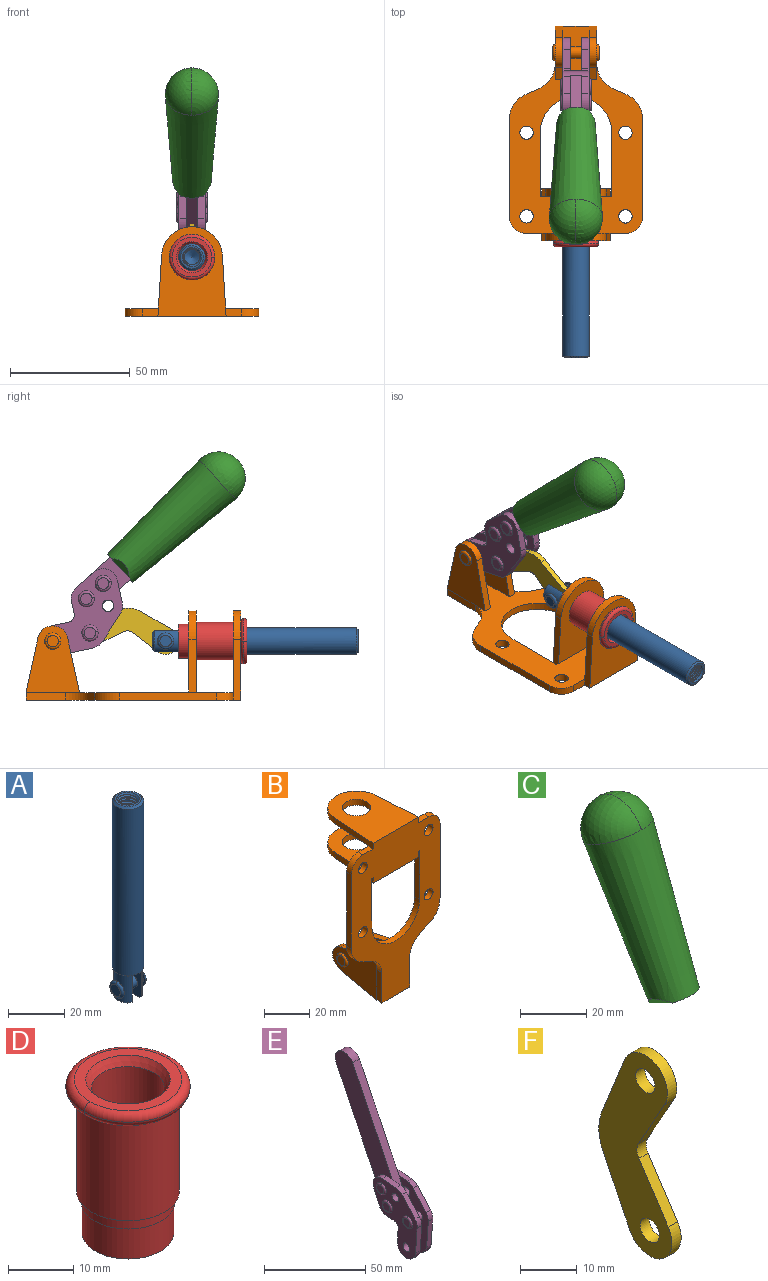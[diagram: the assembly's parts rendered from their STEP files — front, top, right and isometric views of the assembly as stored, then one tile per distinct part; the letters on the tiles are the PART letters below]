
ASSEMBLY  parts=6 mates=6
PART A: 48 faces, bbox 12.6x11.1x86.1 mm
  f0: torus R=2.41mm, axis (-1,0,0), area 15mm2, adj f30,f32,f34
  f1: torus R=2.41mm, axis (-1,0,0), area 15mm2, adj f29,f31,f33
  f2: cylinder r=5.54mm len=72.39mm, axis (0,0,1), area 2518.5mm2, adj f3,f4,f42,f43
  f3: cone r=5.54mm half-angle=45deg, axis (0,0,1), area 7.6mm2, adj f2,f5,f41
  f4: cone r=5.54mm half-angle=45deg, axis (0,0,-1), area 34.9mm2, adj f2,f39
  f5: cylinder r=5.08mm len=11.48mm, axis (0,0,1), area 108.3mm2, adj f3,f7,f8,f41
  f6: cylinder r=2.41mm len=4.83mm, axis (-1,0,0), area 71.2mm2, adj f40,f41
  f7: cylinder r=2.41mm len=4.83mm, axis (-1,0,0), area 7.6mm2, adj f5,f34
  f8: cone r=5.08mm half-angle=45deg, axis (0,0,1), area 10.6mm2, adj f5,f37,f41
  f9: cone r=3.98mm half-angle=45deg, axis (0,0,1), area 17.6mm2, adj f27,f39,f45,f46,f47
  f10: cylinder r=2.41mm len=4.83mm, axis (-1,0,0), area 7.6mm2, adj f33,f38
  f11: cylinder r=3.2mm len=6.4mm, axis (0,0,1), area 78.4mm2, adj f12,f28,f44,f45,f47
  f12: cylinder r=3.2mm len=6.4mm, axis (0,0,1), area 10.5mm2, adj f11,f13,f45,f47
  f13: cylinder r=3.2mm len=6.4mm, axis (0,0,1), area 10.5mm2, adj f12,f14,f45,f47
  f14: cylinder r=3.2mm len=6.4mm, axis (0,0,1), area 10.5mm2, adj f13,f15,f45,f47
  f15: cylinder r=3.2mm len=6.4mm, axis (0,0,1), area 10.5mm2, adj f14,f16,f45,f47
  f16: cylinder r=3.2mm len=6.4mm, axis (0,0,1), area 10.5mm2, adj f15,f17,f45,f47
  f17: cylinder r=3.2mm len=6.4mm, axis (0,0,1), area 10.5mm2, adj f16,f18,f45,f47
  f18: cylinder r=3.2mm len=6.4mm, axis (0,0,1), area 10.5mm2, adj f17,f19,f45,f47
  f19: cylinder r=3.2mm len=6.4mm, axis (0,0,1), area 10.5mm2, adj f18,f20,f45,f47
  f20: cylinder r=3.2mm len=6.4mm, axis (0,0,1), area 10.5mm2, adj f19,f21,f45,f47
  f21: cylinder r=3.2mm len=6.4mm, axis (0,0,1), area 10.5mm2, adj f20,f22,f45,f47
  f22: cylinder r=3.2mm len=6.4mm, axis (0,0,1), area 10.5mm2, adj f21,f23,f45,f47
  f23: cylinder r=3.2mm len=6.4mm, axis (0,0,1), area 10.5mm2, adj f22,f24,f45,f47
  f24: cylinder r=3.2mm len=6.4mm, axis (0,0,1), area 10.5mm2, adj f23,f25,f45,f47
  f25: cylinder r=3.2mm len=6.4mm, axis (0,0,1), area 10.5mm2, adj f24,f26,f45,f47
  f26: cylinder r=3.2mm len=6.4mm, axis (0,0,1), area 10.5mm2, adj f25,f27,f45,f47
  f27: cylinder r=3.2mm len=6.4mm, axis (0,0,1), area 7.4mm2, adj f9,f26,f45,f47
  f28: cone r=3.2mm half-angle=60deg, axis (0,0,1), area 37.2mm2, adj f11
  f29: plane 4.83x4.83mm, normal (-1,0,0), area 18.3mm2, adj f1,f31
  f30: plane 4.83x4.83mm, normal (1,0,0), area 18.3mm2, adj f0,f32
  f31: torus R=2.41mm, axis (-1,0,0), area 15mm2, adj f1,f29,f33
  f32: torus R=2.41mm, axis (-1,0,0), area 15mm2, adj f0,f30,f34
  f33: plane 6.83x6.83mm, normal (1,0,0), area 18.3mm2, adj f1,f10,f31
  f34: plane 6.83x6.83mm, normal (-1,0,0), area 18.3mm2, adj f0,f7,f32
  f35: cone r=5.08mm half-angle=45deg, axis (0,0,1), area 10.6mm2, adj f36,f38,f40
  f36: plane 7.25x1.97mm, normal (0,0,-1), area 10mm2, adj f35,f40
  f37: plane 7.25x1.97mm, normal (0,0,-1), area 10mm2, adj f8,f41
  f38: cylinder r=5.08mm len=11.48mm, axis (0,0,1), area 108.3mm2, adj f10,f35,f40,f42
  f39: plane 9.55x9.55mm, normal (0,0,1), area 22mm2, adj f4,f9
  f40: plane 12.76x10.09mm, normal (1,0,0), area 95.7mm2, adj f6,f35,f36,f38,f42,f43
  f41: plane 12.76x10.09mm, normal (-1,0,0), area 95.7mm2, adj f3,f5,f6,f8,f37,f43
  f42: cone r=5.54mm half-angle=45deg, axis (0,0,1), area 7.6mm2, adj f2,f38,f40
  f43: plane 11.07x4.7mm, normal (0,0,-1), area 50.4mm2, adj f2,f40,f41
  f44: plane 0.89x0.62mm, normal (-1,0,0), area 0.3mm2, adj f11,f45,f46,f47
  f45: bspline ~24.8x7.63mm, area 266.6mm2, adj f9,f11,f12,f13,f14,f15,f16,f17
  f46: bspline ~24.87x7.63mm, area 73.6mm2, adj f9,f44,f45,f47
  f47: bspline ~24.98x7.63mm, area 272.5mm2, adj f9,f11,f12,f13,f14,f15,f16,f17
PART B: 55 faces, bbox 55.7x37.4x89.8 mm
  f0: torus R=2.41mm, axis (-1,0,0), area 15mm2, adj f11,f15,f25
  f1: torus R=2.41mm, axis (-1,0,0), area 15mm2, adj f10,f12,f22
  f2: cylinder r=2.78mm len=5.56mm, axis (0,-1,0), area 54.2mm2, adj f30,f54
  f3: cylinder r=14.99mm len=29.97mm, axis (0,-1,0), area 145.9mm2, adj f30,f49,f53,f54
  f4: cylinder r=2.78mm len=5.56mm, axis (0,-1,0), area 54.2mm2, adj f30,f54
  f5: cylinder r=2.78mm len=5.56mm, axis (0,-1,0), area 54.2mm2, adj f30,f54
  f6: cylinder r=2.78mm len=5.56mm, axis (0,-1,0), area 54.2mm2, adj f30,f54
  f7: cylinder r=6.35mm len=12.7mm, axis (0,0,1), area 123.6mm2, adj f27,f51
  f8: cylinder r=6.35mm len=12.7mm, axis (0,0,-1), area 124.7mm2, adj f21,f35
  f9: cylinder r=2.41mm len=11.18mm, axis (-1,0,0), area 169.4mm2, adj f16,f19
  f10: plane 4.83x4.83mm, normal (1,0,0), area 18.3mm2, adj f1,f12
  f11: plane 4.83x4.83mm, normal (-1,0,0), area 18.3mm2, adj f0,f15
  f12: torus R=2.41mm, axis (-1,0,0), area 15mm2, adj f1,f10,f22
  f13: cylinder r=6.35mm len=12.41mm, axis (1,0,0), area 53.4mm2, adj f18,f19,f22,f23
  f14: cylinder r=6.35mm len=12.41mm, axis (-1,0,0), area 53.4mm2, adj f16,f17,f24,f25
  f15: torus R=2.41mm, axis (-1,0,0), area 15mm2, adj f0,f11,f25
  f16: plane 27.86x22.35mm, normal (1,0,0), area 425.4mm2, adj f9,f14,f17,f24,f30
  f17: plane 22.86x4.97mm, normal (0,0.21,0.98), area 72.5mm2, adj f14,f16,f25,f30
  f18: plane 22.86x4.97mm, normal (0,0.21,0.98), area 72.5mm2, adj f13,f19,f22,f30
  f19: plane 27.86x22.35mm, normal (-1,0,0), area 425.4mm2, adj f9,f13,f18,f23,f30
  f20: cylinder r=12.7mm len=25.35mm, axis (0,0,-1), area 119.8mm2, adj f21,f34,f35,f36
  f21: plane 34.21x28.07mm, normal (0,0,-1), area 702.4mm2, adj f8,f20,f30,f34,f36
  f22: plane 27.96x22.45mm, normal (1,0,0), area 407.2mm2, adj f1,f12,f13,f18,f23,f30,f42,f43
  f23: plane 22.86x4.97mm, normal (0,0.21,-0.98), area 72.5mm2, adj f13,f19,f22,f44
  f24: plane 22.86x4.97mm, normal (0,0.21,-0.98), area 72.5mm2, adj f14,f16,f25,f44
  f25: plane 27.86x22.35mm, normal (-1,0,0), area 407.1mm2, adj f0,f14,f15,f17,f24,f30,f45,f46
  f26: plane 3.1x0.95mm, normal (0,0,-1), area 2.7mm2, adj f30,f49,f50,f54
  f27: plane 34.21x28.07mm, normal (0,0,1), area 702.4mm2, adj f7,f28,f30,f50,f52
  f28: cylinder r=12.7mm len=25.35mm, axis (0,0,1), area 118.8mm2, adj f27,f50,f51,f52
  f29: plane 3.1x0.95mm, normal (0,0,-1), area 2.7mm2, adj f30,f52,f53,f54
  f30: plane 86.54x55.63mm, normal (0,1,0), area 2362.9mm2, adj f2,f3,f4,f5,f6,f16,f17,f18
  f31: plane 40.56x3.1mm, normal (-1,0,0), area 125.7mm2, adj f30,f32,f48,f54
  f32: cylinder r=7.11mm len=7.11mm, axis (0,-1,0), area 34.6mm2, adj f30,f31,f33,f54
  f33: plane 6.67x3.1mm, normal (0,0,1), area 20.4mm2, adj f30,f32,f34,f54
  f34: plane 25.39x3.13mm, normal (-1,0.06,0), area 79.5mm2, adj f20,f21,f33,f35,f54
  f35: plane 37.31x28.45mm, normal (0,0,1), area 789.9mm2, adj f8,f20,f34,f36,f54
  f36: plane 25.39x3.13mm, normal (1,0.06,0), area 79.5mm2, adj f20,f21,f35,f37,f54
  f37: plane 6.67x3.1mm, normal (0,0,1), area 20.4mm2, adj f30,f36,f38,f54
  f38: cylinder r=7.11mm len=7.11mm, axis (0,-1,0), area 34.6mm2, adj f30,f37,f39,f54
  f39: plane 40.56x3.1mm, normal (1,0,0), area 125.7mm2, adj f30,f38,f40,f54
  f40: cylinder r=11.18mm len=10.16mm, axis (0,-1,0), area 39.5mm2, adj f30,f39,f41,f54
  f41: plane 6.09x3.1mm, normal (0.42,0,-0.91), area 20.8mm2, adj f30,f40,f42,f54
  f42: cylinder r=11.18mm len=9.41mm, axis (0,-1,0), area 37.2mm2, adj f22,f30,f41,f43,f54
  f43: plane 16.5x3.1mm, normal (1,0,0), area 51.1mm2, adj f22,f42,f44,f54
  f44: plane 17.37x3.1mm, normal (0,0,-1), area 53.8mm2, adj f23,f24,f30,f43,f45,f54
  f45: plane 16.5x3.1mm, normal (-1,0,0), area 51.1mm2, adj f25,f44,f46,f54
  f46: cylinder r=11.18mm len=9.41mm, axis (0,-1,0), area 37.2mm2, adj f25,f30,f45,f47,f54
  f47: plane 6.09x3.1mm, normal (-0.42,0,-0.91), area 20.8mm2, adj f30,f46,f48,f54
  f48: cylinder r=11.18mm len=10.16mm, axis (0,-1,0), area 39.5mm2, adj f30,f31,f47,f54
  f49: plane 26.54x3.1mm, normal (-1,0,0), area 82.3mm2, adj f3,f26,f30,f54
  f50: plane 25.39x3.1mm, normal (1,0.06,0), area 78.8mm2, adj f26,f27,f28,f51,f54
  f51: plane 37.31x28.45mm, normal (0,0,-1), area 789.9mm2, adj f7,f28,f50,f52,f54
  f52: plane 25.39x3.1mm, normal (-1,0.06,0), area 78.8mm2, adj f27,f28,f29,f51,f54
  f53: plane 26.54x3.1mm, normal (1,0,0), area 82.3mm2, adj f3,f29,f30,f54
  f54: plane 89.66x55.63mm, normal (0,-1,0), area 2678.5mm2, adj f2,f3,f4,f5,f6,f26,f29,f31
PART C: 11 faces, bbox 22.3x42.6x64.5 mm
  f0: sphere r=11.13mm, area 411.4mm2, adj f1,f8
  f1: cone r=11.11mm half-angle=3.3deg, axis (0,0.44,0.9), area 3251.8mm2, adj f0,f7,f8,f9,f10
  f2: cylinder r=6.16mm len=11.7mm, axis (1,0,0), area 89.5mm2, adj f3,f4,f5,f6
  f3: plane 60.23x36.75mm, normal (-1,0,0), area 763.6mm2, adj f2,f4,f6,f10
  f4: plane 51.37x25.05mm, normal (0,0.9,-0.44), area 264.2mm2, adj f2,f3,f5,f10
  f5: plane 60.23x36.75mm, normal (1,0,0), area 763.6mm2, adj f2,f4,f6,f10
  f6: plane 51.37x25.05mm, normal (0,-0.9,0.44), area 264.2mm2, adj f2,f3,f5,f10
  f7: plane 9.95x5.95mm, normal (0.71,-0.31,-0.64), area 25.8mm2, adj f1,f10
  f8: sphere r=11.13mm, area 411.4mm2, adj f0,f1
  f9: plane 9.95x5.95mm, normal (-0.71,-0.31,-0.64), area 25.8mm2, adj f1,f10
  f10: plane 14.27x11.38mm, normal (0,-0.44,-0.9), area 106.7mm2, adj f1,f3,f4,f5,f6,f7,f9
PART D: 15 faces, bbox 20.6x20.6x28.7 mm
  f0: torus R=8.26mm, axis (0,0,1), area 56.8mm2, adj f1,f10,f12
  f1: torus R=8.26mm, axis (0,0,1), area 56.8mm2, adj f0,f6,f13
  f2: cylinder r=5.59mm len=25.91mm, axis (0,0,1), area 909.6mm2, adj f3,f4
  f3: cone r=6.86mm half-angle=45deg, axis (0,0,-1), area 70.2mm2, adj f2,f14
  f4: cone r=6.47mm half-angle=30deg, axis (0,0,1), area 66.7mm2, adj f2,f13
  f5: cylinder r=7.04mm len=14.07mm, axis (0,0,1), area 252.6mm2, adj f11,f14
  f6: torus R=8.26mm, axis (0,0,1), area 56.8mm2, adj f1,f12,f13
  f7: cylinder r=7.16mm len=14.33mm, axis (0,0,1), area 91.5mm2, adj f9,f11
  f8: cylinder r=7.86mm len=18.42mm, axis (0,0,1), area 909.6mm2, adj f9,f10
  f9: plane 15.72x15.72mm, normal (0,0,-1), area 33mm2, adj f7,f8
  f10: plane 16.51x16.51mm, normal (0,0,-1), area 19.9mm2, adj f0,f8,f12
  f11: plane 14.33x14.33mm, normal (0,0,-1), area 5.7mm2, adj f5,f7
  f12: torus R=8.26mm, axis (0,0,1), area 56.8mm2, adj f0,f6,f10
  f13: plane 16.51x16.51mm, normal (0,0,1), area 82.7mm2, adj f1,f4,f6
  f14: plane 14.07x14.07mm, normal (0,0,-1), area 7.8mm2, adj f3,f5
PART E: 59 faces, bbox 12.9x60.2x99.6 mm
  f0: torus R=2.39mm, axis (-1,0,0), area 14.9mm2, adj f20,f43,f51
  f1: torus R=2.39mm, axis (-1,0,0), area 14.9mm2, adj f19,f42,f51
  f2: torus R=2.39mm, axis (-1,0,0), area 14.9mm2, adj f18,f35,f51
  f3: torus R=2.39mm, axis (-1,0,0), area 14.9mm2, adj f14,f17,f23
  f4: torus R=2.39mm, axis (-1,0,0), area 14.9mm2, adj f13,f16,f23
  f5: torus R=2.39mm, axis (-1,0,0), area 14.9mm2, adj f12,f15,f23
  f6: cylinder r=2.39mm len=4.78mm, axis (1,0,0), area 46.5mm2, adj f48,f50,f51
  f7: cylinder r=2.39mm len=4.78mm, axis (1,0,0), area 46.5mm2, adj f50,f51
  f8: cylinder r=6.35mm len=12.68mm, axis (1,0,0), area 61.8mm2, adj f38,f39,f50,f51
  f9: cylinder r=2.39mm len=4.78mm, axis (-1,0,0), area 70.5mm2, adj f46,f50
  f10: cylinder r=2.39mm len=4.78mm, axis (-1,0,0), area 46.5mm2, adj f23,f45,f46
  f11: cylinder r=2.39mm len=4.78mm, axis (-1,0,0), area 46.5mm2, adj f23,f46
  f12: plane 4.78x4.78mm, normal (1,0,0), area 17.9mm2, adj f5,f15
  f13: plane 4.78x4.78mm, normal (1,0,0), area 17.9mm2, adj f4,f16
  f14: plane 4.78x4.78mm, normal (1,0,0), area 17.9mm2, adj f3,f17
  f15: torus R=2.39mm, axis (-1,0,0), area 14.9mm2, adj f5,f12,f23
  f16: torus R=2.39mm, axis (-1,0,0), area 14.9mm2, adj f4,f13,f23
  f17: torus R=2.39mm, axis (-1,0,0), area 14.9mm2, adj f3,f14,f23
  f18: plane 4.78x4.78mm, normal (-1,0,0), area 17.9mm2, adj f2,f35
  f19: plane 4.78x4.78mm, normal (-1,0,0), area 17.9mm2, adj f1,f42
  f20: plane 4.78x4.78mm, normal (-1,0,0), area 17.9mm2, adj f0,f43
  f21: plane 2.26x0.2mm, normal (1,0,0), area 0.2mm2, adj f31,f44
  f22: plane 2.26x0.2mm, normal (-1,0,0), area 0.2mm2, adj f41,f44
  f23: plane 39.37x30.77mm, normal (1,0,0), area 565.5mm2, adj f3,f4,f5,f10,f11,f15,f16,f17
  f24: cylinder r=6.1mm len=4.15mm, axis (-1,0,0), area 14.7mm2, adj f23,f25,f32,f46
  f25: plane 10.25x9.01mm, normal (0,-0.75,0.66), area 42.3mm2, adj f23,f24,f26,f46
  f26: cylinder r=6.35mm len=4.64mm, axis (-1,0,0), area 15.6mm2, adj f23,f25,f27,f46
  f27: plane 15.84x3.1mm, normal (0,-1,-0.07), area 49.2mm2, adj f23,f26,f28,f46
  f28: cylinder r=6.35mm len=12.68mm, axis (-1,0,0), area 61.8mm2, adj f23,f27,f29,f46
  f29: plane 8.11x3.1mm, normal (0,1,0.07), area 25.2mm2, adj f23,f28,f30,f46
  f30: cylinder r=3.05mm len=3.25mm, axis (-1,0,0), area 14.8mm2, adj f23,f29,f31,f46
  f31: plane 5.99x3.1mm, normal (0,0.07,-1), area 18.6mm2, adj f21,f23,f30,f44,f46
  f32: plane 9.5x3.1mm, normal (0,-0.07,1), area 29.5mm2, adj f23,f24,f33,f46,f47
  f33: cylinder r=6.1mm len=8.63mm, axis (-1,0,0), area 39.1mm2, adj f23,f32,f34,f47
  f34: plane 8.65x3.96mm, normal (0,0.91,-0.42), area 29.5mm2, adj f23,f33,f44,f47
  f35: torus R=2.39mm, axis (-1,0,0), area 14.9mm2, adj f2,f18,f51
  f36: plane 10.25x9.01mm, normal (0,-0.75,0.66), area 42.3mm2, adj f37,f49,f50,f51
  f37: cylinder r=6.35mm len=4.64mm, axis (1,0,0), area 15.6mm2, adj f36,f38,f50,f51
  f38: plane 15.84x3.1mm, normal (0,-1,-0.07), area 49.2mm2, adj f8,f37,f50,f51
  f39: plane 8.11x3.1mm, normal (0,1,0.07), area 25.2mm2, adj f8,f40,f50,f51
  f40: cylinder r=3.05mm len=3.25mm, axis (1,0,0), area 14.8mm2, adj f39,f41,f50,f51
  f41: plane 5.99x3.1mm, normal (0,0.07,-1), area 18.6mm2, adj f22,f40,f44,f50,f51
  f42: torus R=2.39mm, axis (-1,0,0), area 14.9mm2, adj f1,f19,f51
  f43: torus R=2.39mm, axis (-1,0,0), area 14.9mm2, adj f0,f20,f51
  f44: cylinder r=6.35mm len=12.12mm, axis (-1,0,0), area 128.9mm2, adj f21,f22,f23,f31,f34,f41,f46,f47
  f45: plane 2.65x1.35mm, normal (1,0,0), area 1mm2, adj f10,f55
  f46: plane 39.08x20.42mm, normal (-1,0,0), area 412.5mm2, adj f9,f10,f11,f24,f25,f26,f27,f28
  f47: plane 77.62x39.82mm, normal (1,0,0), area 850mm2, adj f32,f33,f34,f44,f53,f54,f55
  f48: plane 2.65x1.35mm, normal (-1,0,0), area 1mm2, adj f6,f55
  f49: cylinder r=6.1mm len=4.15mm, axis (1,0,0), area 14.7mm2, adj f36,f50,f51,f56
  f50: plane 39.08x20.42mm, normal (1,0,0), area 412.5mm2, adj f6,f7,f8,f9,f36,f37,f38,f39
  f51: plane 39.37x30.77mm, normal (-1,0,0), area 565.5mm2, adj f0,f1,f2,f6,f7,f8,f35,f36
  f52: plane 8.65x3.96mm, normal (0,0.91,-0.42), area 29.5mm2, adj f44,f51,f57,f58
  f53: plane 68.49x33.4mm, normal (0,0.9,-0.44), area 358.1mm2, adj f44,f47,f54,f58
  f54: cylinder r=6.35mm len=12.06mm, axis (1,0,0), area 93.7mm2, adj f47,f53,f55,f58
  f55: plane 68.49x33.4mm, normal (0,-0.9,0.44), area 358.1mm2, adj f44,f45,f46,f47,f48,f50,f54,f58
  f56: plane 9.5x3.1mm, normal (0,-0.07,1), area 29.5mm2, adj f49,f50,f51,f57,f58
  f57: cylinder r=6.1mm len=8.63mm, axis (1,0,0), area 39.1mm2, adj f51,f52,f56,f58
  f58: plane 77.62x39.82mm, normal (-1,0,0), area 850mm2, adj f44,f52,f53,f54,f55,f56,f57
PART F: 12 faces, bbox 2.3x18.2x42.8 mm
  f0: cylinder r=2.4mm len=4.8mm, axis (1,0,0), area 34.9mm2, adj f4,f11
  f1: cylinder r=10.41mm len=8.47mm, axis (1,0,0), area 20.2mm2, adj f4,f9,f10,f11
  f2: cylinder r=3.05mm len=3.16mm, axis (1,0,0), area 7.7mm2, adj f4,f6,f7,f11
  f3: cylinder r=2.4mm len=4.8mm, axis (1,0,0), area 34.9mm2, adj f4,f11
  f4: plane 42.81x18.23mm, normal (-1,0,0), area 414.1mm2, adj f0,f1,f2,f3,f5,f6,f7,f8
  f5: cylinder r=5.54mm len=10.67mm, axis (1,0,0), area 41.8mm2, adj f4,f6,f10,f11
  f6: plane 11.66x6.53mm, normal (0,-0.87,-0.49), area 30.9mm2, adj f2,f4,f5,f11
  f7: plane 11.17x7.33mm, normal (0,-0.84,0.55), area 30.9mm2, adj f2,f4,f8,f11
  f8: cylinder r=5.54mm len=10.51mm, axis (1,0,0), area 41.8mm2, adj f4,f7,f9,f11
  f9: plane 13.67x6.67mm, normal (0,0.9,-0.44), area 35.1mm2, adj f1,f4,f8,f11
  f10: plane 14.1x5.7mm, normal (0,0.93,0.37), area 35.1mm2, adj f1,f4,f5,f11
  f11: plane 42.81x18.23mm, normal (1,0,0), area 414.1mm2, adj f0,f1,f2,f3,f5,f6,f7,f8
PLACE A rot(axis=(1,0,0),90deg) t=(0,9.63,0)mm
PLACE B rot(axis=(1,0,0),90deg) t=(0,9.14,0)mm fixed
PLACE C rot(axis=(1,0,0),73.7deg) t=(-0.04,3.52,9.99)mm
PLACE D rot(axis=(1,0,0),90deg) t=(0,9.14,0)mm
PLACE E rot(axis=(1,0,0),73.7deg) t=(0,3.52,9.99)mm
PLACE F rot(axis=(1,0,0),98.1deg) t=(0,12.94,2.43)mm
MATE slider A.f2 <-> D.f2  axis (0,-1,0) through (0,-49.15,24.61)mm
MATE fastened D.f2 <-> B.f7  axis (0,-1,0) through (0,-37.25,24.61)mm
MATE revolute F.f3 <-> E.f4  axis (1,0,0) through (0,25.72,27.99)mm
MATE revolute F.f5 <-> A.f6  axis (1,0,0) through (0,-5.85,24.61)mm
MATE fastened C.f2 <-> E.f54  axis (1,0,0) through (-2.35,-29.12,93.54)mm
MATE revolute E.f7 <-> B.f0  axis (-1,0,0) through (0,41.23,24.61)mm
